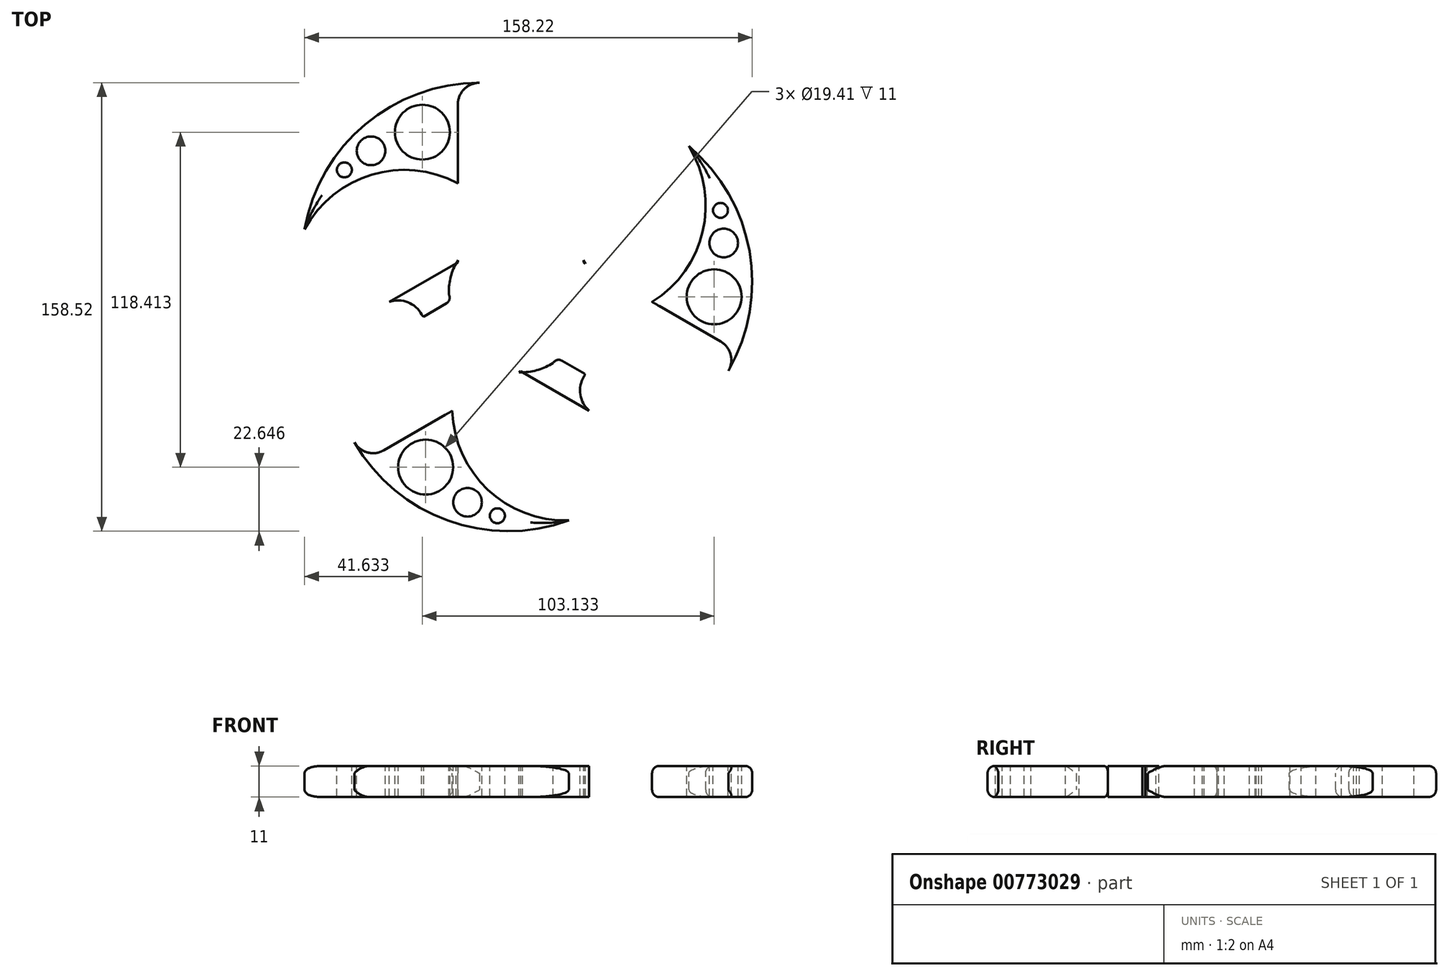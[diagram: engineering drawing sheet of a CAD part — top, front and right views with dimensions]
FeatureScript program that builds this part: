
annotation { "Feature Type Name" : "Feature", "Feature Type Description" : "" }
export const myFeature = defineFeature(function(context is Context, id is Id, definition is map)
    precondition{}
    {
        {
            var Q0;
            Q0=qCreatedBy(makeId("Top.planeOp"),FACE);
            var sketch = newSketch(context, id + "F0", { "sketchPlane" : qUnion([Q0])});
            skCircle(sketch, "E0.cCircle", {"center": v(0, 0) * mm, "radius": 12.83 * mm, "construction": true});
            skLineSegment(sketch, "E0.0", {"start": v(-22.22, 12.83) * mm, "end": v(22.22, 12.83) * mm});
            skLineSegment(sketch, "E0.1", {"start": v(22.23, 12.83) * mm, "end": v(0, -25.66) * mm});
            skLineSegment(sketch, "E0.2", {"start": v(0, -25.66) * mm, "end": v(-22.23, 12.83) * mm});
            skPoint(sketch, "E0.0.midPoint", {"position": v(0, 12.83) * mm});
            skSolve(sketch);
        }
        {
            var Q0;
            Q0=qSketchRegion(id+"F0",true);
            extrude(context, id + "F1", {"entities" : qUnion([Q0]), "depth" : 11 * mm, "offsetDistance" : 25.4 * mm});
        }
        {
            var Q0;
            Q0=makeQuery(id+"F1.opExtrude","SWEPT_FACE",FACE,{"disambiguationData":[OSD([sQuery(id+"F0.wireOp",EDGE,"E0.2")])]});
            extrude(context, id + "F2", {"entities" : qUnion([Q0]), "operationType" : NewBodyOperationType.ADD, "depth" : 63.5 * mm, "offsetDistance" : 25.4 * mm});
        }
        {
            var Q0;
            Q0=makeQuery(id+"F1.opExtrude","SWEPT_FACE",FACE,{"disambiguationData":[OSD([sQuery(id+"F0.wireOp",EDGE,"E0.0")])]});
            extrude(context, id + "F3", {"entities" : qUnion([Q0]), "operationType" : NewBodyOperationType.ADD, "depth" : 63.5 * mm, "offsetDistance" : 25.4 * mm});
        }
        {
            var Q0;
            Q0=makeQuery(id+"F1.opExtrude","SWEPT_FACE",FACE,{"disambiguationData":[OSD([sQuery(id+"F0.wireOp",EDGE,"E0.1")])]});
            extrude(context, id + "F4", {"entities" : qUnion([Q0]), "operationType" : NewBodyOperationType.ADD, "depth" : 63.5 * mm, "offsetDistance" : 25.4 * mm});
        }
        {
            var Q0;
            {var subQ0=sQuery(id+"F0.wireOp",EDGE,"E0.1");var subQ1=sQuery(id+"F0.wireOp",EDGE,"E0.0");var subQ2=sQuery(id+"F0.wireOp",EDGE,"E0.2");Q0=makeQuery(id+"F4.boolean.opBoolean","MERGE",FACE,{"derivedFrom":[makeQuery(id+"F3.boolean.opBoolean","MERGE",FACE,{"derivedFrom":[makeQuery(id+"F2.boolean.opBoolean","MERGE",FACE,{"derivedFrom":[makeQuery(id+"F1.opExtrude","CAP_FACE",FACE,{"disambiguationData":[OSD([subQ1,subQ0,subQ2])],"isStart":false}),makeQuery(id+"F2.opExtrude","SWEPT_FACE",FACE,{"disambiguationData":[OSD([subQ2]),TDD([makeQuery(id+"F1.opExtrude","CAP_EDGE",EDGE,{"disambiguationData":[OSD([subQ2])],"isStart":false})])]})]}),makeQuery(id+"F3.opExtrude","SWEPT_FACE",FACE,{"disambiguationData":[OSD([subQ1]),TDD([makeQuery(id+"F1.opExtrude","CAP_EDGE",EDGE,{"disambiguationData":[OSD([subQ1])],"isStart":false})])]})]}),makeQuery(id+"F4.opExtrude","SWEPT_FACE",FACE,{"disambiguationData":[OSD([subQ0]),TDD([makeQuery(id+"F1.opExtrude","CAP_EDGE",EDGE,{"disambiguationData":[OSD([subQ0])],"isStart":false})])]})]});}
            var sketch = newSketch(context, id + "F5", { "sketchPlane" : qUnion([Q0])});
            skPoint(sketch, "E1", {"position": v(0, 76.33) * mm});
            skPoint(sketch, "E2", {"position": v(66.1, -38.17) * mm});
            skPoint(sketch, "E3", {"position": v(-66.1, -38.17) * mm});
            skLineSegment(sketch, "E4", {"start": v(0, 76.33) * mm, "end": v(0, 54.1) * mm});
            skLineSegment(sketch, "E5", {"start": v(66.1, -38.17) * mm, "end": v(46.86, -27.05) * mm});
            skLineSegment(sketch, "E6", {"start": v(-66.1, -38.17) * mm, "end": v(-46.86, -27.05) * mm});
            skCircle(sketch, "E7", {"center": v(-46.86, -27.05) * mm, "radius": 17.5 * mm});
            skCircle(sketch, "E8", {"center": v(0, 54.1) * mm, "radius": 17.5 * mm});
            skCircle(sketch, "E9", {"center": v(46.86, -27.05) * mm, "radius": 17.5 * mm});
            skCircle(sketch, "E10", {"center": v(0, 0) * mm, "radius": 17.5 * mm});
            skSolve(sketch);
        }
        {
            var Q0;
            Q0=makeQuery(id+"F2.opExtrude","CAP_EDGE",EDGE,{"disambiguationData":[OSD([sQuery(id+"F0.wireOp",EDGE,"E0.0"),sQuery(id+"F0.wireOp",EDGE,"E0.2")])],"isStart":false});
            var Q1;
            Q1=makeQuery(id+"F2.opExtrude","CAP_EDGE",EDGE,{"disambiguationData":[OSD([sQuery(id+"F0.wireOp",EDGE,"E0.1"),sQuery(id+"F0.wireOp",EDGE,"E0.2")])],"isStart":false});
            var Q2;
            Q2=makeQuery(id+"F4.opExtrude","CAP_EDGE",EDGE,{"disambiguationData":[OSD([sQuery(id+"F0.wireOp",EDGE,"E0.1"),sQuery(id+"F0.wireOp",EDGE,"E0.2")])],"isStart":false});
            var Q3;
            Q3=makeQuery(id+"F4.opExtrude","CAP_EDGE",EDGE,{"disambiguationData":[OSD([sQuery(id+"F0.wireOp",EDGE,"E0.0"),sQuery(id+"F0.wireOp",EDGE,"E0.1")])],"isStart":false});
            var Q4;
            Q4=makeQuery(id+"F3.opExtrude","CAP_EDGE",EDGE,{"disambiguationData":[OSD([sQuery(id+"F0.wireOp",EDGE,"E0.0"),sQuery(id+"F0.wireOp",EDGE,"E0.1")])],"isStart":false});
            var Q5;
            Q5=makeQuery(id+"F3.opExtrude","CAP_EDGE",EDGE,{"disambiguationData":[OSD([sQuery(id+"F0.wireOp",EDGE,"E0.0"),sQuery(id+"F0.wireOp",EDGE,"E0.2")])],"isStart":false});
            fillet(context, id + "F6", {"entities" : qUnion([Q0, Q1, Q2, Q3, Q4, Q5]), "radius" : 7.62 * mm, "tangentPropagation" : true, "allowEdgeOverflow" : false});
        }
        {
            var Q0;
            Q0=makeQuery(id+"F5.imprint","IMPRINT",FACE,{"disambiguationData":[TD([[makeQuery(id+"F5.imprint","IMPRINT",EDGE,{"derivedFrom":sQuery(id+"F5.wireOp",EDGE,"E7")}),1.0]])]});
            var Q1;
            Q1=makeQuery(id+"F5.imprint","IMPRINT",FACE,{"disambiguationData":[TD([[makeQuery(id+"F5.imprint","IMPRINT",EDGE,{"derivedFrom":sQuery(id+"F5.wireOp",EDGE,"E10")}),1.0]])]});
            var Q2;
            Q2=makeQuery(id+"F5.imprint","IMPRINT",FACE,{"disambiguationData":[TD([[makeQuery(id+"F5.imprint","IMPRINT",EDGE,{"derivedFrom":sQuery(id+"F5.wireOp",EDGE,"E9")}),1.0]])]});
            var Q3;
            Q3=makeQuery(id+"F5.imprint","IMPRINT",FACE,{"disambiguationData":[TD([[makeQuery(id+"F5.imprint","IMPRINT",EDGE,{"derivedFrom":sQuery(id+"F5.wireOp",EDGE,"E8")}),1.0]])]});
            extrude(context, id + "F7", {"entities" : qUnion([Q0, Q1, Q2, Q3]), "operationType" : NewBodyOperationType.REMOVE, "oppositeDirection" : true, "depth" : 25.4 * mm, "offsetDistance" : 25.4 * mm});
        }
        {
            var Q0;
            {var subQ0=sQuery(id+"F0.wireOp",EDGE,"E0.1");var subQ1=sQuery(id+"F0.wireOp",EDGE,"E0.0");var subQ2=sQuery(id+"F0.wireOp",EDGE,"E0.2");Q0=makeQuery(id+"F4.boolean.opBoolean","MERGE",FACE,{"derivedFrom":[makeQuery(id+"F3.boolean.opBoolean","MERGE",FACE,{"derivedFrom":[makeQuery(id+"F2.boolean.opBoolean","MERGE",FACE,{"derivedFrom":[makeQuery(id+"F1.opExtrude","CAP_FACE",FACE,{"disambiguationData":[OSD([subQ1,subQ0,subQ2])],"isStart":false}),makeQuery(id+"F2.opExtrude","SWEPT_FACE",FACE,{"disambiguationData":[OSD([subQ2]),TDD([makeQuery(id+"F1.opExtrude","CAP_EDGE",EDGE,{"disambiguationData":[OSD([subQ2])],"isStart":false})])]})]}),makeQuery(id+"F3.opExtrude","SWEPT_FACE",FACE,{"disambiguationData":[OSD([subQ1]),TDD([makeQuery(id+"F1.opExtrude","CAP_EDGE",EDGE,{"disambiguationData":[OSD([subQ1])],"isStart":false})])]})]}),makeQuery(id+"F4.opExtrude","SWEPT_FACE",FACE,{"disambiguationData":[OSD([subQ0]),TDD([makeQuery(id+"F1.opExtrude","CAP_EDGE",EDGE,{"disambiguationData":[OSD([subQ0])],"isStart":false})])]})]});}
            var sketch = newSketch(context, id + "F8", { "sketchPlane" : qUnion([Q0])});
            skArc(sketch, "E11", {"start": v(-14.6, 76.33) * mm, "mid": v(-54.94, 61.65) * mm, "end": v(-76.4, 24.48) * mm});
            skArc(sketch, "E12", {"start": v(-22.22, 40.77) * mm, "mid": v(-52.68, 43.83) * mm, "end": v(-76.4, 24.48) * mm});
            skPoint(sketch, "E13.center", {"position": v(0, 0) * mm});
            skCircle(sketch, "E14", {"center": v(-34.77, 58.87) * mm, "radius": 9.7 * mm});
            skCircle(sketch, "E15", {"center": v(-52.91, 52.27) * mm, "radius": 5.06 * mm});
            skCircle(sketch, "E16", {"center": v(-62.34, 45.53) * mm, "radius": 2.64 * mm});
            skArc(sketch, "E17.1.0", {"start": v(-24.2, -39.63) * mm, "mid": v(-11.62, -67.54) * mm, "end": v(17, -78.4) * mm});
            skCircle(sketch, "E17.1.1", {"center": v(-33.6, -59.54) * mm, "radius": 9.7 * mm});
            skArc(sketch, "E17.1.2", {"start": v(-58.8, -50.81) * mm, "mid": v(-25.92, -78.4) * mm, "end": v(17, -78.4) * mm});
            skCircle(sketch, "E17.1.3", {"center": v(-18.8, -71.96) * mm, "radius": 5.06 * mm});
            skCircle(sketch, "E17.1.4", {"center": v(-8.26, -76.75) * mm, "radius": 2.64 * mm});
            skArc(sketch, "E17.2.0", {"start": v(46.42, -1.14) * mm, "mid": v(64.3, 23.71) * mm, "end": v(59.4, 53.93) * mm});
            skCircle(sketch, "E17.2.1", {"center": v(68.37, 0.68) * mm, "radius": 9.7 * mm});
            skArc(sketch, "E17.2.2", {"start": v(73.4, -25.52) * mm, "mid": v(80.86, 16.75) * mm, "end": v(59.4, 53.93) * mm});
            skCircle(sketch, "E17.2.3", {"center": v(71.72, 19.69) * mm, "radius": 5.06 * mm});
            skCircle(sketch, "E17.2.4", {"center": v(70.6, 31.22) * mm, "radius": 2.64 * mm});
            skSolve(sketch);
        }
        {
            var Q0;
            {var subQ0=sQuery(id+"F0.wireOp",EDGE,"E0.2");var subQ1=sQuery(id+"F0.wireOp",EDGE,"E0.1");var subQ2=sQuery(id+"F0.wireOp",EDGE,"E0.0");Q0=makeQuery(id+"FOKae3Fr5oamKkQ_1.opFillet","SPLIT",FACE,{"disambiguationData":[OD(6.0)],"derivedFrom":makeQuery(id+"FG1d5Ig31lzTRB0_1.boolean.opBoolean","MERGE",FACE,{"derivedFrom":[makeQuery(id+"F4.boolean.opBoolean","MERGE",FACE,{"derivedFrom":[makeQuery(id+"F3.boolean.opBoolean","MERGE",FACE,{"derivedFrom":[makeQuery(id+"F2.boolean.opBoolean","MERGE",FACE,{"derivedFrom":[makeQuery(id+"F1.opExtrude","CAP_FACE",FACE,{"disambiguationData":[OSD([subQ2,subQ1,subQ0])],"isStart":false}),makeQuery(id+"F2.opExtrude","SWEPT_FACE",FACE,{"disambiguationData":[OSD([subQ0]),TDD([makeQuery(id+"F1.opExtrude","CAP_EDGE",EDGE,{"disambiguationData":[OSD([subQ0])],"isStart":false})])]})]}),makeQuery(id+"F3.opExtrude","SWEPT_FACE",FACE,{"disambiguationData":[OSD([subQ2]),TDD([makeQuery(id+"F1.opExtrude","CAP_EDGE",EDGE,{"disambiguationData":[OSD([subQ2])],"isStart":false})])]})]}),makeQuery(id+"F4.opExtrude","SWEPT_FACE",FACE,{"disambiguationData":[OSD([subQ1]),TDD([makeQuery(id+"F1.opExtrude","CAP_EDGE",EDGE,{"disambiguationData":[OSD([subQ1])],"isStart":false})])]})]}),makeQuery(id+"FG1d5Ig31lzTRB0_1.opExtrude","CAP_FACE",FACE,{"disambiguationData":[OSD([subQ2,subQ1,subQ0,sQuery(id+"F8.wireOp",EDGE,"E11"),sQuery(id+"F8.wireOp",EDGE,"E12"),sQuery(id+"F8.wireOp",EDGE,"NNQIrfYk-JMjS-KAwr-kWHs-Bf6wTVIj3mDU"),sQuery(id+"F8.wireOp",EDGE,"45iQ7aQf-pqhX-wCj4-ZdGj-3CdDhslE9RYF"),sQuery(id+"F8.wireOp",EDGE,"NPk8IUMQ-wFkR-c8GS-j7AI-E4jGxeNdETuf")])],"isStart":true}),makeQuery(id+"FG1d5Ig31lzTRB0_1.opExtrude","CAP_FACE",FACE,{"disambiguationData":[OSD([subQ2,subQ1,subQ0,sQuery(id+"F8.wireOp",EDGE,"E13.1.0"),sQuery(id+"F8.wireOp",EDGE,"E13.1.1"),sQuery(id+"F8.wireOp",EDGE,"E13.1.2"),sQuery(id+"F8.wireOp",EDGE,"E13.1.3"),sQuery(id+"F8.wireOp",EDGE,"E13.1.4")])],"isStart":true}),makeQuery(id+"FG1d5Ig31lzTRB0_1.opExtrude","CAP_FACE",FACE,{"disambiguationData":[OSD([subQ2,subQ1,subQ0,sQuery(id+"F8.wireOp",EDGE,"E13.2.0"),sQuery(id+"F8.wireOp",EDGE,"E13.2.1"),sQuery(id+"F8.wireOp",EDGE,"E13.2.2"),sQuery(id+"F8.wireOp",EDGE,"E13.2.3"),sQuery(id+"F8.wireOp",EDGE,"E13.2.4")])],"isStart":true})]})});}
            var sketch = newSketch(context, id + "F9", { "sketchPlane" : qUnion([Q0])});
            skLineSegment(sketch, "E18", {"start": v(-11.68, 32.81) * mm, "end": v(-11.68, 23.6) * mm});
            skLineSegment(sketch, "E19.MirrorCS", {"start": v(11.68, 32.81) * mm, "end": v(11.68, 23.6) * mm});
            skPoint(sketch, "E20.center", {"position": v(0, 0) * mm});
            skArc(sketch, "E21", {"start": v(-22.22, 40.77) * mm, "mid": v(-18.84, 35.17) * mm, "end": v(-12.62, 33.12) * mm});
            skArc(sketch, "E22.MirrorCS", {"start": v(22.22, 40.77) * mm, "mid": v(18.84, 35.17) * mm, "end": v(12.62, 33.12) * mm});
            skArc(sketch, "E23", {"start": v(-11.68, 32.81) * mm, "mid": v(-12.11, 33.07) * mm, "end": v(-12.62, 33.12) * mm});
            skArc(sketch, "E24.MirrorCS", {"start": v(11.68, 32.81) * mm, "mid": v(12.11, 33.07) * mm, "end": v(12.62, 33.12) * mm});
            skArc(sketch, "E25", {"start": v(-13.94, 21.28) * mm, "mid": v(-12.34, 21.99) * mm, "end": v(-11.68, 23.6) * mm});
            skArc(sketch, "E26.MirrorCS", {"start": v(13.94, 21.28) * mm, "mid": v(12.34, 21.99) * mm, "end": v(11.68, 23.6) * mm});
            skArc(sketch, "E27.1.0", {"start": v(-24.2, -39.63) * mm, "mid": v(-21.04, -33.9) * mm, "end": v(-22.38, -27.49) * mm});
            skArc(sketch, "E27.1.1", {"start": v(-22.58, -26.52) * mm, "mid": v(-22.59, -27.03) * mm, "end": v(-22.38, -27.49) * mm});
            skLineSegment(sketch, "E27.1.2", {"start": v(-22.58, -26.52) * mm, "end": v(-14.6, -21.92) * mm});
            skArc(sketch, "E27.1.3", {"start": v(-11.46, -22.7) * mm, "mid": v(-12.87, -21.68) * mm, "end": v(-14.6, -21.92) * mm});
            skArc(sketch, "E27.1.4", {"start": v(-46.42, -1.14) * mm, "mid": v(-39.88, -1.27) * mm, "end": v(-35, -5.63) * mm});
            skArc(sketch, "E27.1.5", {"start": v(-34.26, -6.3) * mm, "mid": v(-34.7, -6.05) * mm, "end": v(-35, -5.63) * mm});
            skLineSegment(sketch, "E27.1.6", {"start": v(-34.26, -6.3) * mm, "end": v(-26.28, -1.69) * mm});
            skArc(sketch, "E27.1.7", {"start": v(-25.4, 1.43) * mm, "mid": v(-25.2, -0.3) * mm, "end": v(-26.28, -1.69) * mm});
            skArc(sketch, "E27.2.0", {"start": v(46.42, -1.14) * mm, "mid": v(39.88, -1.27) * mm, "end": v(35, -5.63) * mm});
            skArc(sketch, "E27.2.1", {"start": v(34.26, -6.3) * mm, "mid": v(34.7, -6.05) * mm, "end": v(35, -5.63) * mm});
            skLineSegment(sketch, "E27.2.2", {"start": v(34.26, -6.3) * mm, "end": v(26.28, -1.69) * mm});
            skArc(sketch, "E27.2.3", {"start": v(25.4, 1.43) * mm, "mid": v(25.2, -0.3) * mm, "end": v(26.28, -1.69) * mm});
            skArc(sketch, "E27.2.4", {"start": v(24.2, -39.63) * mm, "mid": v(21.04, -33.9) * mm, "end": v(22.38, -27.49) * mm});
            skArc(sketch, "E27.2.5", {"start": v(22.58, -26.52) * mm, "mid": v(22.59, -27.03) * mm, "end": v(22.38, -27.49) * mm});
            skLineSegment(sketch, "E27.2.6", {"start": v(22.58, -26.52) * mm, "end": v(14.6, -21.92) * mm});
            skArc(sketch, "E27.2.7", {"start": v(11.46, -22.7) * mm, "mid": v(12.87, -21.68) * mm, "end": v(14.6, -21.92) * mm});
            skArc(sketch, "E28", {"start": v(-13.94, 21.28) * mm, "mid": v(-22.57, 13.03) * mm, "end": v(-25.4, 1.43) * mm});
            skArc(sketch, "E29.1.0", {"start": v(-11.46, -22.7) * mm, "mid": v(0, -26.06) * mm, "end": v(11.46, -22.7) * mm});
            skArc(sketch, "E29.2.0", {"start": v(25.4, 1.43) * mm, "mid": v(22.57, 13.03) * mm, "end": v(13.94, 21.28) * mm});
            skSolve(sketch);
        }
        {
            var Q0;
            Q0=makeQuery(id+"F8.imprint","IMPRINT",FACE,{"disambiguationData":[TD([[makeQuery(id+"F8.imprint","IMPRINT",EDGE,{"derivedFrom":sQuery(id+"F8.wireOp",EDGE,"E11")}),1.0]])]});
            var Q1;
            {var subQ4=sQuery(id+"F8.wireOp",EDGE,"E17.1.0");Q1=makeQuery(id+"F8.imprint","IMPRINT",FACE,{"disambiguationData":[TD([[makeQuery(id+"F8.imprint","IMPRINT",EDGE,{"derivedFrom":subQ4}),-1.0]])]});}
            var Q2;
            {var subQ0=sQuery(id+"F8.wireOp",EDGE,"E17.2.0");Q2=makeQuery(id+"F8.imprint","IMPRINT",FACE,{"disambiguationData":[TD([[makeQuery(id+"F8.imprint","IMPRINT",EDGE,{"derivedFrom":subQ0}),-1.0]])]});}
            extrude(context, id + "F10", {"entities" : qUnion([Q0, Q1, Q2]), "operationType" : NewBodyOperationType.ADD, "oppositeDirection" : true, "depth" : 11 * mm, "offsetDistance" : 25.4 * mm});
        }
        {
            var Q0;
            {var subQ0=sQuery(id+"F9.wireOp",EDGE,"E28");var subQ1=sQuery(id+"F0.wireOp",EDGE,"E0.2");var subQ2=sQuery(id+"F0.wireOp",EDGE,"E0.0");var subQ3=makeQuery(id+"F1.opExtrude","CAP_VERTEX",VERTEX,{"disambiguationData":[OSD([subQ2,subQ1])],"isStart":false});var subQ6=makeQuery(id+"F2.opExtrude","SWEPT_EDGE",EDGE,{"disambiguationData":[OSD([subQ2,subQ1]),TDD([subQ3])]});var subQ7=makeQuery(id+"F9.imprint","INTERSECT",VERTEX,{"derivedFrom":[subQ6,subQ0]});Q0=makeQuery(id+"F9.imprint","IMPRINT",FACE,{"disambiguationData":[TD([[makeQuery(id+"F9.imprint","IMPRINT",EDGE,{"disambiguationData":[TD([[subQ7,1.0]])],"derivedFrom":subQ0}),1.0]])]});}
            var Q1;
            {var subQ0=sQuery(id+"F9.wireOp",EDGE,"E29.1.0");var subQ1=sQuery(id+"F0.wireOp",EDGE,"E0.2");var subQ2=sQuery(id+"F0.wireOp",EDGE,"E0.1");var subQ3=makeQuery(id+"F1.opExtrude","CAP_VERTEX",VERTEX,{"disambiguationData":[OSD([subQ2,subQ1])],"isStart":false});var subQ4=makeQuery(id+"F2.opExtrude","SWEPT_EDGE",EDGE,{"disambiguationData":[OSD([subQ2,subQ1]),TDD([subQ3])]});var subQ5=makeQuery(id+"F9.imprint","INTERSECT",VERTEX,{"derivedFrom":[subQ4,subQ0]});Q1=makeQuery(id+"F9.imprint","IMPRINT",FACE,{"disambiguationData":[TD([[makeQuery(id+"F9.imprint","IMPRINT",EDGE,{"disambiguationData":[TD([[subQ5,-1.0]])],"derivedFrom":subQ0}),1.0]])]});}
            var Q2;
            {var subQ0=sQuery(id+"F9.wireOp",EDGE,"E29.2.0");var subQ1=sQuery(id+"F0.wireOp",EDGE,"E0.1");var subQ2=sQuery(id+"F0.wireOp",EDGE,"E0.0");var subQ3=makeQuery(id+"F1.opExtrude","CAP_VERTEX",VERTEX,{"disambiguationData":[OSD([subQ2,subQ1])],"isStart":false});var subQ6=makeQuery(id+"F3.opExtrude","SWEPT_EDGE",EDGE,{"disambiguationData":[OSD([subQ2,subQ1]),TDD([subQ3])]});var subQ7=makeQuery(id+"F9.imprint","INTERSECT",VERTEX,{"derivedFrom":[subQ6,subQ0]});Q2=makeQuery(id+"F9.imprint","IMPRINT",FACE,{"disambiguationData":[TD([[makeQuery(id+"F9.imprint","IMPRINT",EDGE,{"disambiguationData":[TD([[subQ7,1.0]])],"derivedFrom":subQ0}),1.0]])]});}
            extrude(context, id + "F11", {"entities" : qUnion([Q0, Q1, Q2]), "operationType" : NewBodyOperationType.ADD, "oppositeDirection" : true, "depth" : 11 * mm, "offsetDistance" : 25.4 * mm});
        }
        {
            var Q0;
            {var subQ6=sQuery(id+"F9.wireOp",EDGE,"E27.1.4");Q0=makeQuery(id+"F9.imprint","IMPRINT",FACE,{"disambiguationData":[TD([[makeQuery(id+"F9.imprint","IMPRINT",EDGE,{"derivedFrom":subQ6}),1.0]])]});}
            var Q1;
            Q1=makeQuery(id+"F9.imprint","IMPRINT",FACE,{"disambiguationData":[TD([[makeQuery(id+"F9.imprint","IMPRINT",EDGE,{"derivedFrom":sQuery(id+"F9.wireOp",EDGE,"E18")}),-1.0]])]});
            var Q2;
            Q2=makeQuery(id+"F9.imprint","IMPRINT",FACE,{"disambiguationData":[TD([[makeQuery(id+"F9.imprint","IMPRINT",EDGE,{"derivedFrom":sQuery(id+"F9.wireOp",EDGE,"E19.MirrorCS")}),1.0]])]});
            var Q3;
            {var subQ7=sQuery(id+"F9.wireOp",EDGE,"E27.2.0");Q3=makeQuery(id+"F9.imprint","IMPRINT",FACE,{"disambiguationData":[TD([[makeQuery(id+"F9.imprint","IMPRINT",EDGE,{"derivedFrom":subQ7}),-1.0]])]});}
            var Q4;
            {var subQ1=sQuery(id+"F9.wireOp",EDGE,"E27.2.4");Q4=makeQuery(id+"F9.imprint","IMPRINT",FACE,{"disambiguationData":[TD([[makeQuery(id+"F9.imprint","IMPRINT",EDGE,{"derivedFrom":subQ1}),1.0]])]});}
            var Q5;
            {var subQ1=sQuery(id+"F9.wireOp",EDGE,"E27.1.0");Q5=makeQuery(id+"F9.imprint","IMPRINT",FACE,{"disambiguationData":[TD([[makeQuery(id+"F9.imprint","IMPRINT",EDGE,{"derivedFrom":subQ1}),-1.0]])]});}
            extrude(context, id + "F12", {"entities" : qUnion([Q0, Q1, Q2, Q3, Q4, Q5]), "operationType" : NewBodyOperationType.REMOVE, "oppositeDirection" : true, "depth" : 25.4 * mm, "offsetDistance" : 25.4 * mm});
        }
        {
            var Q0;
            Q0=makeQuery(id+"F10.opExtrude","CAP_EDGE",EDGE,{"disambiguationData":[OSD([sQuery(id+"F8.wireOp",EDGE,"E12")])],"isStart":true});
            var Q1;
            Q1=makeQuery(id+"F10.opExtrude","CAP_EDGE",EDGE,{"disambiguationData":[OSD([sQuery(id+"F8.wireOp",EDGE,"E11")])],"isStart":true});
            var Q2;
            Q2=makeQuery(id+"F10.opExtrude","CAP_EDGE",EDGE,{"disambiguationData":[OSD([sQuery(id+"F8.wireOp",EDGE,"E12")])],"isStart":false});
            var Q3;
            Q3=makeQuery(id+"F10.opExtrude","CAP_EDGE",EDGE,{"disambiguationData":[OSD([sQuery(id+"F8.wireOp",EDGE,"E11")])],"isStart":false});
            var Q4;
            Q4=makeQuery(id+"F10.opExtrude","CAP_EDGE",EDGE,{"disambiguationData":[OSD([sQuery(id+"F8.wireOp",EDGE,"E17.1.0")])],"isStart":true});
            var Q5;
            Q5=makeQuery(id+"F10.opExtrude","CAP_EDGE",EDGE,{"disambiguationData":[OSD([sQuery(id+"F8.wireOp",EDGE,"E17.1.0")])],"isStart":false});
            var Q6;
            Q6=makeQuery(id+"F10.opExtrude","CAP_EDGE",EDGE,{"disambiguationData":[OSD([sQuery(id+"F8.wireOp",EDGE,"E17.1.2")])],"isStart":true});
            var Q7;
            Q7=makeQuery(id+"F10.opExtrude","CAP_EDGE",EDGE,{"disambiguationData":[OSD([sQuery(id+"F8.wireOp",EDGE,"E17.1.2")])],"isStart":false});
            var Q8;
            Q8=makeQuery(id+"F10.opExtrude","CAP_EDGE",EDGE,{"disambiguationData":[OSD([sQuery(id+"F8.wireOp",EDGE,"E17.2.2")])],"isStart":true});
            var Q9;
            Q9=makeQuery(id+"F10.opExtrude","CAP_EDGE",EDGE,{"disambiguationData":[OSD([sQuery(id+"F8.wireOp",EDGE,"E17.2.2")])],"isStart":false});
            var Q10;
            Q10=makeQuery(id+"F10.opExtrude","CAP_EDGE",EDGE,{"disambiguationData":[OSD([sQuery(id+"F8.wireOp",EDGE,"E17.2.0")])],"isStart":false});
            var Q11;
            Q11=makeQuery(id+"F10.opExtrude","CAP_EDGE",EDGE,{"disambiguationData":[OSD([sQuery(id+"F8.wireOp",EDGE,"E17.2.0")])],"isStart":true});
            fillet(context, id + "F13", {"entities" : qUnion([Q0, Q1, Q2, Q3, Q4, Q5, Q6, Q7, Q8, Q9, Q10, Q11]), "radius" : 2.54 * mm, "tangentPropagation" : true, "allowEdgeOverflow" : false});
        }
    });
